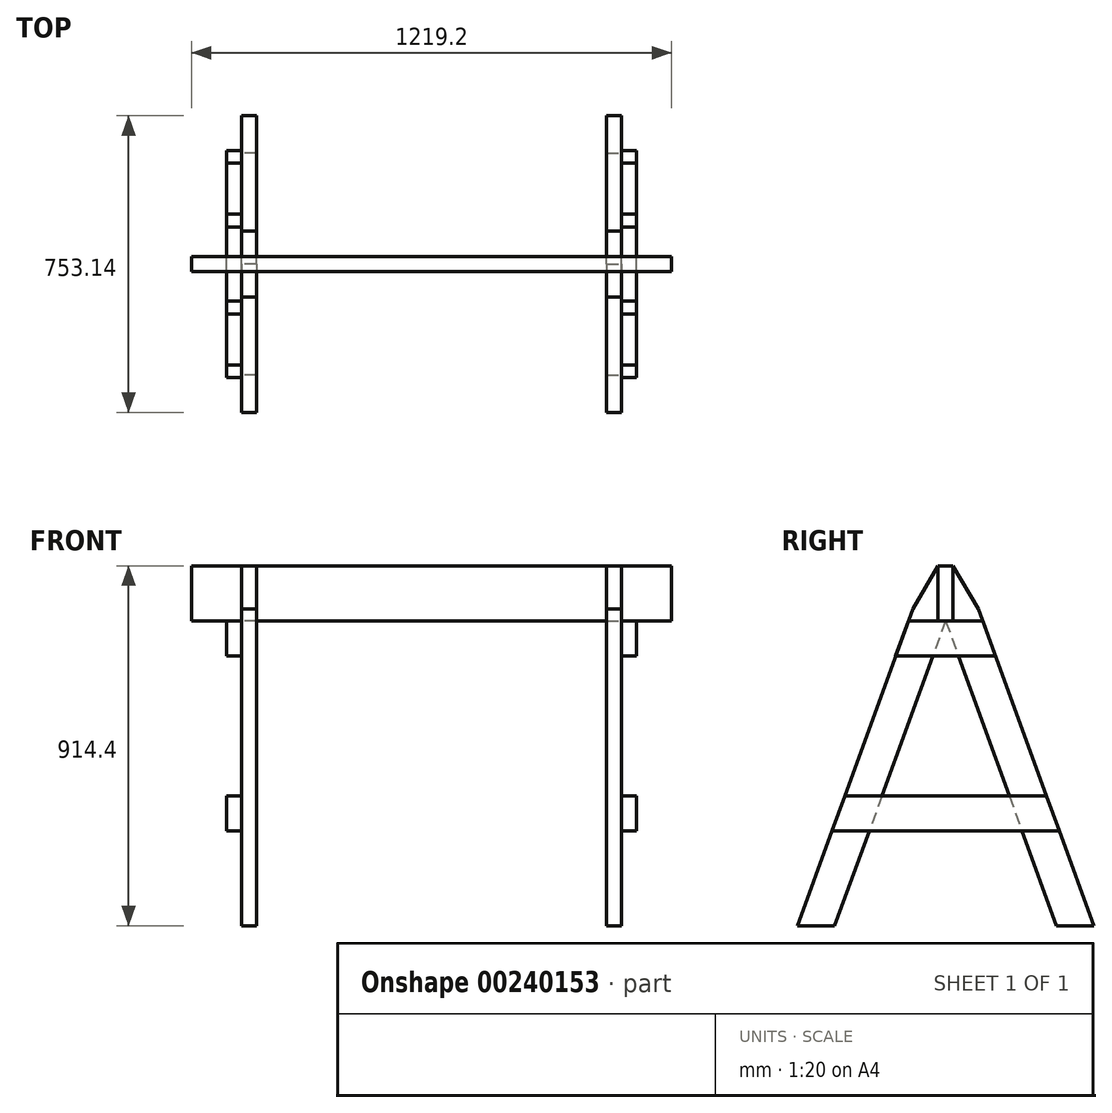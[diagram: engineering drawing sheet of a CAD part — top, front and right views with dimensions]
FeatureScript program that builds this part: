
annotation { "Feature Type Name" : "Feature", "Feature Type Description" : "" }
export const myFeature = defineFeature(function(context is Context, id is Id, definition is map)
    precondition{}
    {
        {
            var Q0;
            Q0=qCreatedBy(makeId("Top.planeOp"),FACE);
            var sketch = newSketch(context, id + "F0", { "sketchPlane" : qUnion([Q0])});
            skLineSegment(sketch, "E0.0", {"start": v(0, -19.05) * mm, "end": v(609.6, -19.05) * mm});
            skLineSegment(sketch, "E0.1", {"start": v(0, -19.05) * mm, "end": v(-609.6, -19.05) * mm});
            skLineSegment(sketch, "E1.0", {"start": v(0, 19.05) * mm, "end": v(609.6, 19.05) * mm});
            skLineSegment(sketch, "E1.1", {"start": v(0, 19.05) * mm, "end": v(-609.6, 19.05) * mm});
            skLineSegment(sketch, "E2", {"start": v(609.6, 19.05) * mm, "end": v(609.6, -19.05) * mm});
            skLineSegment(sketch, "E3", {"start": v(-609.6, 19.05) * mm, "end": v(-609.6, -19.05) * mm});
            skSolve(sketch);
        }
        {
            var Q0;
            Q0 = qSketchRegion(id + "F0", true);
            extrude(context, id + "F1", {"entities" : qUnion([Q0]), "oppositeDirection" : true, "depth" : 139.7 * mm});
        }
        {
            var Q0;
            Q0=makeQuery(id+"F1.opExtrude","SWEPT_FACE",FACE,{"disambiguationData":[OSD([sQuery(id+"F0.wireOp",EDGE,"E3")])]});
            cPlane(context, id + "F2", {"entities" : qUnion([Q0]), "cplaneType" : CPlaneType.OFFSET, "offset" : 146.05 * mm, "oppositeDirection" : true, "width" : 152.4 * mm, "height" : 152.4 * mm});
        }
        {
            var Q0;
            Q0=qCreatedBy(id+"F2.planeOp",FACE);
            var sketch = newSketch(context, id + "F3", { "sketchPlane" : qUnion([Q0])});
            skLineSegment(sketch, "E4", {"start": v(0, 0) * mm, "end": v(0, -914.4) * mm, "construction": true});
            skLineSegment(sketch, "E5", {"start": v(0, -914.4) * mm, "end": v(762, -914.4) * mm, "construction": true});
            skPoint(sketch, "E6.start.orphan", {"position": v(19.05, 120.23) * mm});
            skLineSegment(sketch, "E7", {"start": v(0, -139.7) * mm, "end": v(281.97, -914.4) * mm});
            skLineSegment(sketch, "E8", {"start": v(0, -139.7) * mm, "end": v(83.54, -109.3) * mm, "construction": true});
            skLineSegment(sketch, "E9", {"start": v(83.54, -109.3) * mm, "end": v(40.87, 7.94) * mm, "construction": true});
            skLineSegment(sketch, "E10", {"start": v(-19.05, 0) * mm, "end": v(-19.05, -139.7) * mm, "construction": true});
            skLineSegment(sketch, "E11", {"start": v(-19.05, 0) * mm, "end": v(19.05, 0) * mm, "construction": true});
            skLineSegment(sketch, "E12", {"start": v(-19.05, -139.7) * mm, "end": v(19.05, -139.7) * mm, "construction": true});
            skLineSegment(sketch, "E13", {"start": v(19.05, 0) * mm, "end": v(19.05, -139.7) * mm, "construction": true});
            skLineSegment(sketch, "E14", {"start": v(19.05, 0) * mm, "end": v(83.54, -109.3) * mm});
            skLineSegment(sketch, "E15", {"start": v(19.05, 0) * mm, "end": v(19.05, -139.7) * mm});
            skLineSegment(sketch, "E16", {"start": v(0, -139.7) * mm, "end": v(19.05, -139.7) * mm});
            skLineSegment(sketch, "E17", {"start": v(83.54, -109.3) * mm, "end": v(376.57, -914.4) * mm});
            skLineSegment(sketch, "E18", {"start": v(376.57, -914.4) * mm, "end": v(281.97, -914.4) * mm});
            skLineSegment(sketch, "E19", {"start": v(19.05, 0) * mm, "end": v(40.87, 7.94) * mm, "construction": true});
            skLineSegment(sketch, "E20", {"start": v(19.05, 0) * mm, "end": v(-42.67, -22.46) * mm, "construction": true});
            skLineSegment(sketch, "E21", {"start": v(0, -139.7) * mm, "end": v(-42.67, -22.46) * mm, "construction": true});
            skLineSegment(sketch, "E22", {"start": v(376.57, -914.4) * mm, "end": v(293.03, -944.8) * mm, "construction": true});
            skLineSegment(sketch, "E23", {"start": v(281.97, -914.4) * mm, "end": v(293.03, -944.8) * mm, "construction": true});
            skLineSegment(sketch, "E24", {"start": v(-525.54, 0) * mm, "end": v(-563.64, 0) * mm, "construction": true});
            skLineSegment(sketch, "E25", {"start": v(-563.64, 0) * mm, "end": v(-563.64, -139.7) * mm, "construction": true});
            skLineSegment(sketch, "E26", {"start": v(-563.64, -139.7) * mm, "end": v(-525.54, -139.7) * mm, "construction": true});
            skLineSegment(sketch, "E27", {"start": v(-525.54, -139.7) * mm, "end": v(-525.54, 0) * mm, "construction": true});
            skSolve(sketch);
        }
        {
            var Q0;
            Q0 = qSketchRegion(id + "F3", true);
            extrude(context, id + "F4", {"entities" : qUnion([Q0]), "endBound" : BoundingType.SYMMETRIC, "oppositeDirection" : true, "depth" : 38.1 * mm});
        }
        {
            var Q0;
            Q0=makeQuery(id+"F4.opExtrude","SWEPT_BODY",BODY,{"disambiguationData":[OSD([sQuery(id+"F3.wireOp",EDGE,"E7"),sQuery(id+"F3.wireOp",EDGE,"E14"),sQuery(id+"F3.wireOp",EDGE,"E15"),sQuery(id+"F3.wireOp",EDGE,"E16"),sQuery(id+"F3.wireOp",EDGE,"E17"),sQuery(id+"F3.wireOp",EDGE,"E18")])]});
            var Q1;
            Q1=qCreatedBy(makeId("Front.planeOp"),FACE);
            mirror(context, id + "F5", {"entities" : qUnion([Q0]), "mirrorPlane" : qUnion([Q1])});
        }
        {
            var Q0;
            Q0=makeQuery(id+"F4.opExtrude","SWEPT_BODY",BODY,{"disambiguationData":[OSD([sQuery(id+"F3.wireOp",EDGE,"E7"),sQuery(id+"F3.wireOp",EDGE,"E14"),sQuery(id+"F3.wireOp",EDGE,"E15"),sQuery(id+"F3.wireOp",EDGE,"E16"),sQuery(id+"F3.wireOp",EDGE,"E17"),sQuery(id+"F3.wireOp",EDGE,"E18")])]});
            var Q1;
            Q1=makeQuery(id+"F5.opPattern","COPY",BODY,{"derivedFrom":makeQuery(id+"F4.opExtrude","SWEPT_BODY",BODY,{"disambiguationData":[OSD([sQuery(id+"F3.wireOp",EDGE,"E7"),sQuery(id+"F3.wireOp",EDGE,"E14"),sQuery(id+"F3.wireOp",EDGE,"E15"),sQuery(id+"F3.wireOp",EDGE,"E16"),sQuery(id+"F3.wireOp",EDGE,"E17"),sQuery(id+"F3.wireOp",EDGE,"E18")])]}),"instanceName":"1"});
            var Q2;
            Q2=qCreatedBy(makeId("Right.planeOp"),FACE);
            mirror(context, id + "F6", {"entities" : qUnion([Q0, Q1]), "mirrorPlane" : qUnion([Q2])});
        }
        {
            var Q0;
            Q0=makeQuery(id+"F6.opPattern","COPY",FACE,{"derivedFrom":makeQuery(id+"F4.opExtrude","CAP_FACE",FACE,{"disambiguationData":[OSD([sQuery(id+"F3.wireOp",EDGE,"E7"),sQuery(id+"F3.wireOp",EDGE,"E14"),sQuery(id+"F3.wireOp",EDGE,"E15"),sQuery(id+"F3.wireOp",EDGE,"E16"),sQuery(id+"F3.wireOp",EDGE,"E17"),sQuery(id+"F3.wireOp",EDGE,"E18")])],"isStart":true}),"instanceName":"1"});
            var sketch = newSketch(context, id + "F7", { "sketchPlane" : qUnion([Q0])});
            skLineSegment(sketch, "E28.0", {"start": v(-83.54, -109.3) * mm, "end": v(-376.57, -914.4) * mm});
            skLineSegment(sketch, "E29.0", {"start": v(83.54, -109.3) * mm, "end": v(376.57, -914.4) * mm});
            skLineSegment(sketch, "E30.0", {"start": v(19.05, -139.7) * mm, "end": v(-19.05, -139.7) * mm});
            skLineSegment(sketch, "E31", {"start": v(-94.6, -139.7) * mm, "end": v(94.6, -139.7) * mm});
            skLineSegment(sketch, "E32.0", {"start": v(-126.96, -228.6) * mm, "end": v(126.96, -228.6) * mm});
            skLineSegment(sketch, "E33", {"start": v(-94.6, -139.7) * mm, "end": v(-126.96, -228.6) * mm});
            skLineSegment(sketch, "E34", {"start": v(94.6, -139.7) * mm, "end": v(126.96, -228.6) * mm});
            skLineSegment(sketch, "E35.0", {"start": v(-256.4, -584.2) * mm, "end": v(256.4, -584.2) * mm});
            skLineSegment(sketch, "E36.0", {"start": v(-288.75, -673.1) * mm, "end": v(288.75, -673.1) * mm});
            skSolve(sketch);
        }
        {
            var Q0;
            {var subQ0=sQuery(id+"F7.wireOp",EDGE,"E33");Q0=makeQuery(id+"F7.imprint","IMPRINT",FACE,{"disambiguationData":[TD([[makeQuery(id+"F7.imprint","IMPRINT",EDGE,{"derivedFrom":subQ0}),1.0]])]});}
            var Q1;
            {var subQ3=sQuery(id+"F7.wireOp",EDGE,"E34");Q1=makeQuery(id+"F7.imprint","IMPRINT",FACE,{"disambiguationData":[TD([[makeQuery(id+"F7.imprint","IMPRINT",EDGE,{"derivedFrom":subQ3}),-1.0]])]});}
            extrude(context, id + "F8", {"entities" : qUnion([Q0, Q1]), "depth" : 38.1 * mm});
        }
        {
            var Q0;
            {var subQ0=sQuery(id+"F7.wireOp",EDGE,"E35.0");var subQ1=sQuery(id+"F7.wireOp",EDGE,"E28.0");var subQ2=makeQuery(id+"F7.imprint","INTERSECT",VERTEX,{"derivedFrom":[subQ1,subQ0]});Q0=makeQuery(id+"F7.imprint","IMPRINT",FACE,{"disambiguationData":[TD([[makeQuery(id+"F7.imprint","IMPRINT",EDGE,{"disambiguationData":[TD([[subQ2,-1.0]])],"derivedFrom":subQ1}),1.0]])]});}
            var Q1;
            {var subQ0=sQuery(id+"F7.wireOp",EDGE,"E35.0");var subQ1=sQuery(id+"F7.wireOp",EDGE,"E29.0");var subQ2=makeQuery(id+"F7.imprint","INTERSECT",VERTEX,{"derivedFrom":[subQ1,subQ0]});Q1=makeQuery(id+"F7.imprint","IMPRINT",FACE,{"disambiguationData":[TD([[makeQuery(id+"F7.imprint","IMPRINT",EDGE,{"disambiguationData":[TD([[subQ2,-1.0]])],"derivedFrom":subQ1}),-1.0]])]});}
            extrude(context, id + "F9", {"entities" : qUnion([Q0, Q1]), "depth" : 38.1 * mm});
        }
        {
            var Q0;
            Q0=makeQuery(id+"F8.opExtrude","SWEPT_BODY",BODY,{"disambiguationData":[OSD([sQuery(id+"F7.wireOp",EDGE,"E31"),sQuery(id+"F7.wireOp",EDGE,"E32.0"),sQuery(id+"F7.wireOp",EDGE,"E33"),sQuery(id+"F7.wireOp",EDGE,"E34")])]});
            var Q1;
            Q1=makeQuery(id+"F9.opExtrude","SWEPT_BODY",BODY,{"disambiguationData":[OSD([sQuery(id+"F7.wireOp",EDGE,"E28.0"),sQuery(id+"F7.wireOp",EDGE,"E29.0"),sQuery(id+"F7.wireOp",EDGE,"E35.0"),sQuery(id+"F7.wireOp",EDGE,"E36.0")])]});
            var Q2;
            Q2=qCreatedBy(makeId("Right.planeOp"),FACE);
            mirror(context, id + "F10", {"entities" : qUnion([Q0, Q1]), "mirrorPlane" : qUnion([Q2])});
        }
    });
